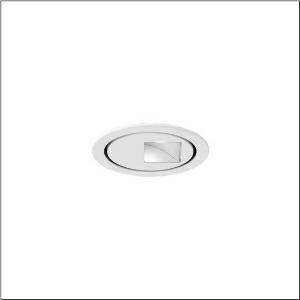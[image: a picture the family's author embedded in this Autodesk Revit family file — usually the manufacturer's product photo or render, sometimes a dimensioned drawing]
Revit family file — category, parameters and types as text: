
# Revit family: lunis_11_micro_round_51dj11b71wm21
name_source: partatom
category: Lighting Fixtures
units: mm (PartAtom-declared; Revit-internal decimal feet)

## family parameters
Cut with Voids When Loaded = No
Host = Face
Light Source = No
Part Type = Normal
Room Calculation Point = No
Round Connector Dimension = Use Diameter
Shared = No

## types (1)
- Lunis 11 micro round (1 x LED 3000K / CRI = 90 (unbekannt), 1100 lm, 3000K)
    Apparent Load = 20 VA
    CIE Flux Codes = 42 75 96 100 100
    Color Rendering = 90
    Color Temperature = 3000K
    Default Elevation = 1800 mm
    Description = Lunis 11 micro round, downlight, light control with wallwasher, of highly reflective aluminium, highly specular, light emission: direct distribution, LED rated luminous flux: 1.100lm, light colour: 930, with terminal, 3-pole, mains connection: 220..230V, AC, 50/60Hz, LED module, of aluminium, highly specular, white, diameter: 114mm, clamping range: 1..40mm, recessing ring, of plastic, traffic white (RAL 9016), protection rating (complete): IP20, insulation class (complete): insulation class II (safety insulation), certification: CE, permissible ambient temperature for indoor applications: 0..+35°C, packaging unit: 1 piece
    Height = 0 mm  [stored 0 ft]
    Lamp = 1 x LED 3000K / CRI >= 90 (unbekannt)
    Lamp Light Flux = 1100 lm
    Lamp count = 1
    Length = 114 mm
    Luminous efficacy = 56 lm/W
    Manufacturer = Siteco
    ModVariant = No
    Model = 51DJ11B71WM21
    Mounting Place = Ceiling
    Mounting Type = Recessed
    Number of Poles = 1
    OnlyDefault = Yes
    Power Factor = 1
    Product Name = Lunis 11 micro round
    Product group = downlight
    ProductGroupID = 401
    Protection Class = Protection class II
    Protection Degree = IP 20
    RLX_Detail_Level = 1
    RLX_Emergency_Light_Flux = 0 lm
    RLX_Emergency_Type = 0
    RLX_Emergency_Type_DB = No
    RlxData = <blob elided: 40209 chars, md5=a15406c1>
    Socket = socket
    Standby Power = 0 W
    System Light Flux = 1100 lm
    System Power = 20 W
    Type Comments = Product without accessories
    Type Image = l_1004773.jpg
    URL = http://relux.com
    VarID = ---
    Voltage = 0 V
    Weight = 0.00 kg
    Width = 114 mm

note: [stored X ft] marks values corroborated as IEEE doubles in the binary element streams (Revit-internal decimal feet)

## geometry (parser evidence)
native form markers: Blend x4, Sweep x9
no freeform markers — native parametric forms only
